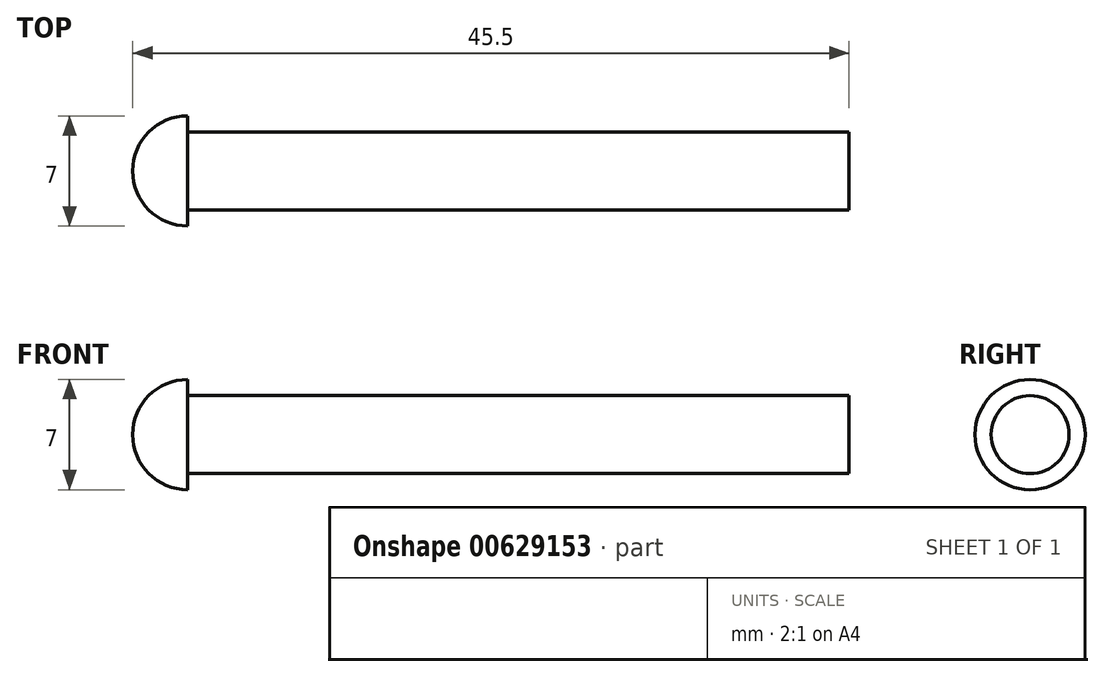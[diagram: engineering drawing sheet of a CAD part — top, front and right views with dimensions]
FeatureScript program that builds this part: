
annotation { "Feature Type Name" : "Feature", "Feature Type Description" : "" }
export const myFeature = defineFeature(function(context is Context, id is Id, definition is map)
    precondition{}
    {
        {
            var Q0;
            Q0=qCreatedBy(makeId("Right.planeOp"),FACE);
            var sketch = newSketch(context, id + "F0", { "sketchPlane" : qUnion([Q0])});
            skCircle(sketch, "E0", {"center": v(0, 0) * mm, "radius": 2.48 * mm});
            skSolve(sketch);
        }
        {
            var Q0;
            Q0=makeQuery(id+"F0.imprint","IMPRINT",FACE,{"disambiguationData":[TD([[makeQuery(id+"F0.imprint","IMPRINT",EDGE,{"derivedFrom":sQuery(id+"F0.wireOp",EDGE,"E0")}),1.0]])]});
            var Q1;
            Q1=sQuery(id+"F0.wireOp",EDGE,"E0");
            extrude(context, id + "F1", {"entities" : qUnion([Q0]), "surfaceEntities" : qUnion([Q1]), "depth" : 42 * mm, "offsetDistance" : 25 * mm});
        }
        {
            var Q0;
            Q0=makeQuery(id+"F1.opExtrude","CAP_FACE",FACE,{"disambiguationData":[OSD([sQuery(id+"F0.wireOp",EDGE,"E0")])],"isStart":true});
            var sketch = newSketch(context, id + "F2", { "sketchPlane" : qUnion([Q0])});
            skLineSegment(sketch, "E1", {"start": v(3.5, 0) * mm, "end": v(-3.5, 0) * mm});
            skArc(sketch, "E2", {"start": v(-3.5, 0) * mm, "mid": v(0, -3.5) * mm, "end": v(3.5, 0) * mm});
            skSolve(sketch);
        }
        {
            var Q0;
            {var subQ0=sQuery(id+"F2.wireOp",EDGE,"E2");Q0=makeQuery(id+"F2.imprint","IMPRINT",FACE,{"disambiguationData":[TD([[makeQuery(id+"F2.imprint","IMPRINT",EDGE,{"derivedFrom":subQ0}),1.0]])]});}
            var Q1;
            {var subQ0=sQuery(id+"F2.wireOp",EDGE,"E1");var subQ1=makeQuery(id+"F1.opExtrude","CAP_EDGE",EDGE,{"disambiguationData":[OSD([sQuery(id+"F0.wireOp",EDGE,"E0")])],"isStart":true});var subQ2=makeQuery(id+"F2.imprint","INTERSECT",VERTEX,{"disambiguationData":[OD(0.0)],"derivedFrom":[subQ1,subQ0]});Q1=makeQuery(id+"F2.imprint","IMPRINT",FACE,{"disambiguationData":[TD([[makeQuery(id+"F2.imprint","IMPRINT",EDGE,{"disambiguationData":[TD([[subQ2,-1.0]])],"derivedFrom":subQ0}),1.0]])]});}
            var Q2;
            Q2=sQuery(id+"F2.wireOp",EDGE,"E1");
            revolve(context, id + "F3", {"operationType" : NewBodyOperationType.ADD, "entities" : qUnion([Q0, Q1]), "axis" : qUnion([Q2]), "revolveType" : RevolveType.ONE_DIRECTION, "angle" : 180 * degree});
        }
    });
